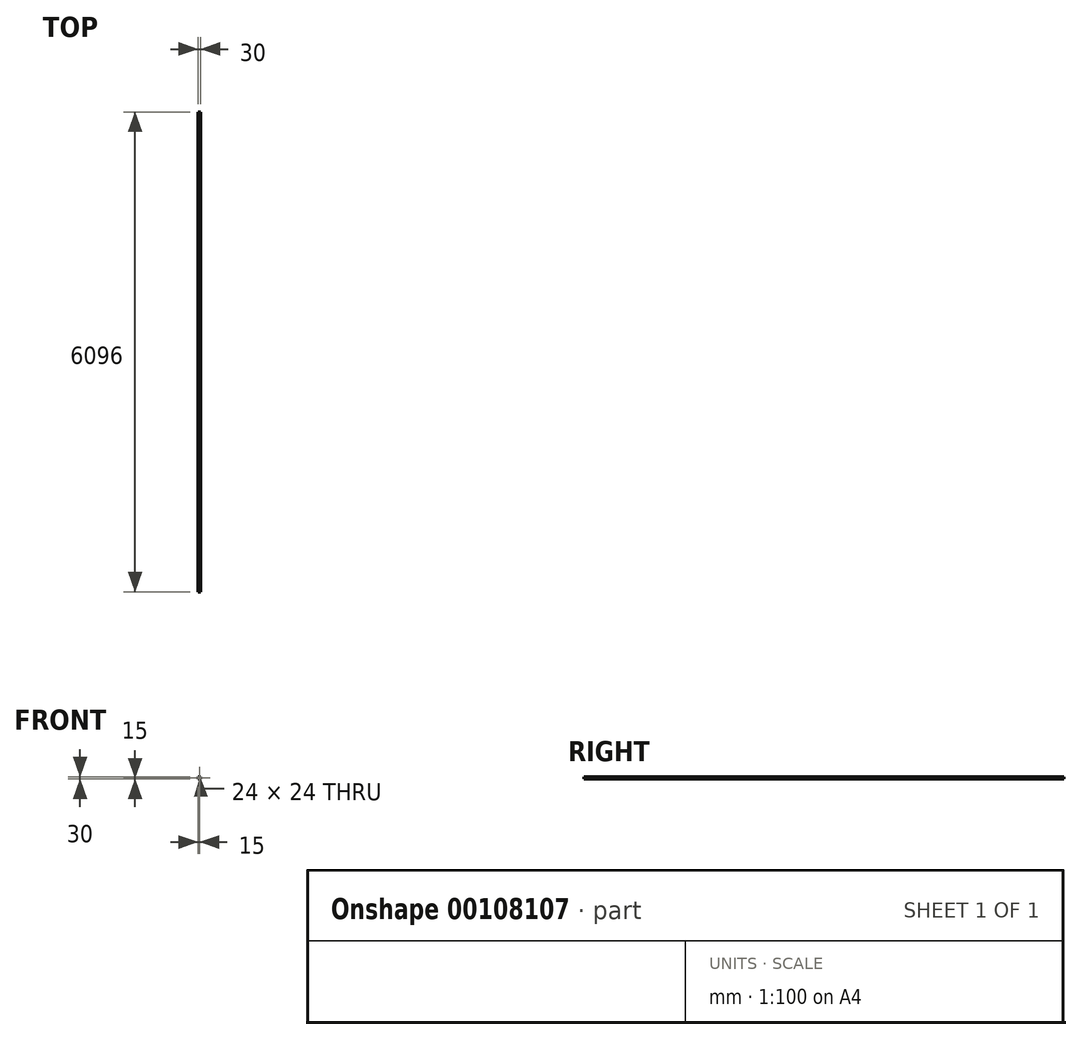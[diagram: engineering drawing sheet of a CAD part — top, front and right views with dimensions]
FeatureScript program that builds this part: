
annotation { "Feature Type Name" : "Feature", "Feature Type Description" : "" }
export const myFeature = defineFeature(function(context is Context, id is Id, definition is map)
    precondition{}
    {
        {
            var Q0;
            Q0=qCreatedBy(makeId("Front.planeOp"),FACE);
            var sketch = newSketch(context, id + "F0", { "sketchPlane" : qUnion([Q0])});
            skLineSegment(sketch, "E0.bottom", {"start": v(15, -15) * mm, "end": v(-15, -15) * mm});
            skLineSegment(sketch, "E0.top", {"start": v(15, 15) * mm, "end": v(-15, 15) * mm});
            skLineSegment(sketch, "E0.left", {"start": v(15, -15) * mm, "end": v(15, 15) * mm});
            skLineSegment(sketch, "E0.right", {"start": v(-15, -15) * mm, "end": v(-15, 15) * mm});
            skPoint(sketch, "E0.middle", {"position": v(0, 0) * mm});
            skLineSegment(sketch, "E1.bottom", {"start": v(12, -12) * mm, "end": v(-12, -12) * mm});
            skLineSegment(sketch, "E1.top", {"start": v(12, 12) * mm, "end": v(-12, 12) * mm});
            skLineSegment(sketch, "E1.left", {"start": v(12, -12) * mm, "end": v(12, 12) * mm});
            skLineSegment(sketch, "E1.right", {"start": v(-12, -12) * mm, "end": v(-12, 12) * mm});
            skSolve(sketch);
        }
        {
            var Q0;
            Q0=makeQuery(id+"F0.imprint","IMPRINT",FACE,{"disambiguationData":[TD([[makeQuery(id+"F0.imprint","IMPRINT",EDGE,{"derivedFrom":sQuery(id+"F0.wireOp",EDGE,"E0.bottom")}),-1.0]])]});
            extrude(context, id + "F1", {"entities" : qUnion([Q0]), "endBound" : BoundingType.SYMMETRIC, "oppositeDirection" : true, "depth" : (5970 + 126) * mm});
        }
    });
